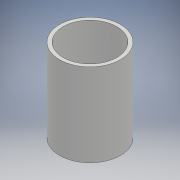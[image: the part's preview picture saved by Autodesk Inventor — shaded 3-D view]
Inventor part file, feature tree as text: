
AUTODESK INVENTOR PART (.ipt)
format: ipt  version: 2017 (Build 210142000, 142)  size: 98,304 bytes
history: native  units: mm
features: extrude x1, sketch x1
ambient origin geometry x8: Origin, YZ Plane, XZ Plane, XY Plane, X Axis, Y Axis, Z Axis, Center Point
bodies: Body1 (feature_tree)
feature tree (2):
  extrude  "Extrusion2"  Depth=30.0mm
  sketch  "Sketch2"  dims[d5=22.0mm d7=1.3mm d8=30.0mm d9=0.0mm]
